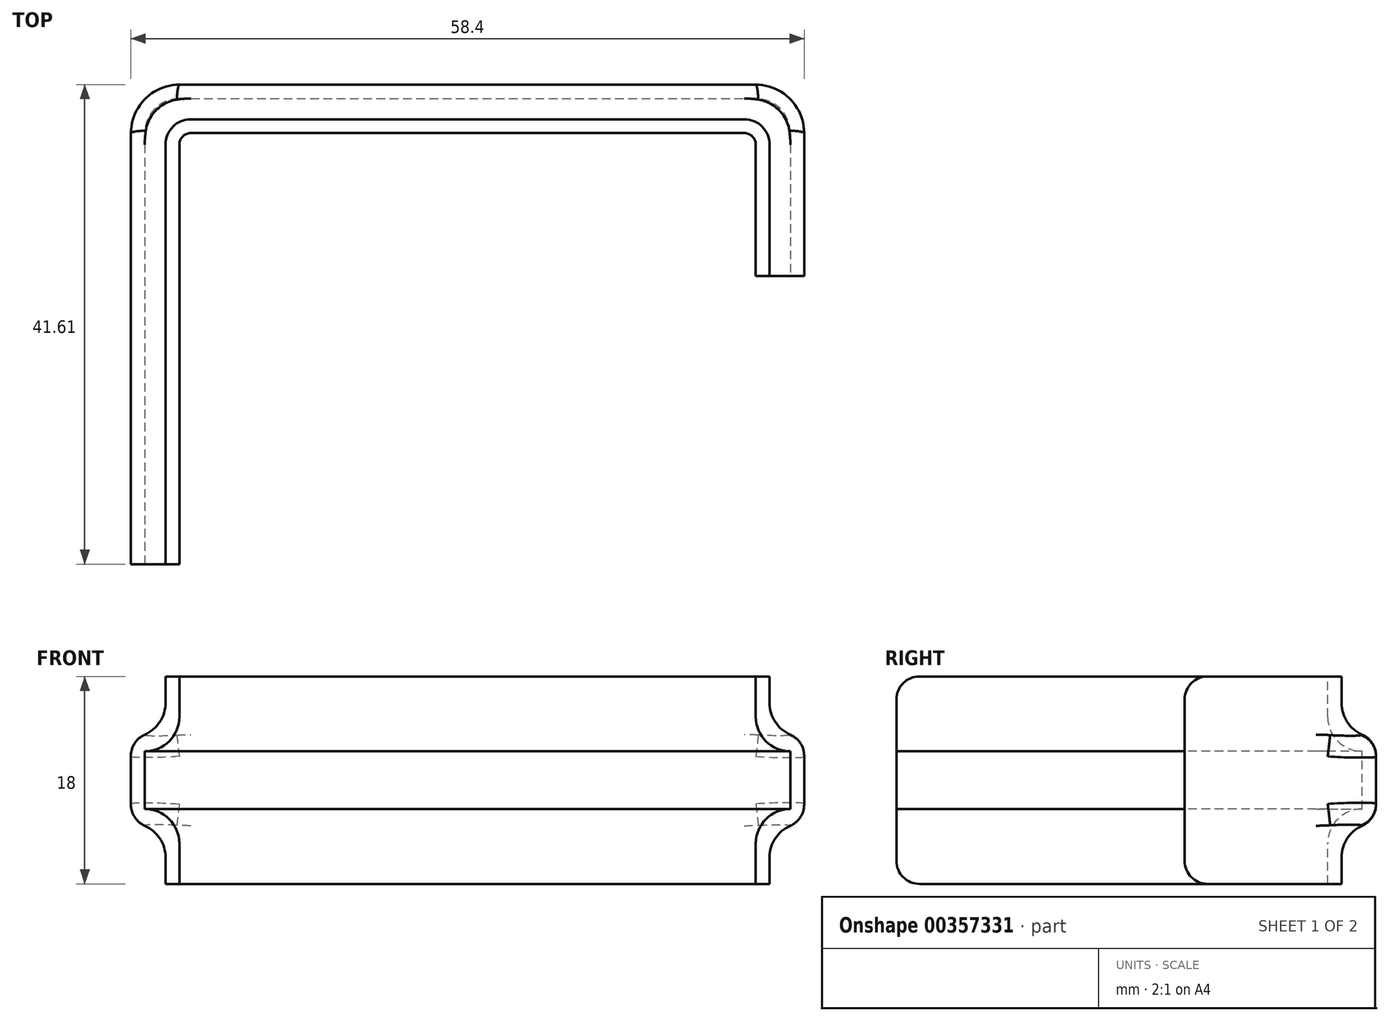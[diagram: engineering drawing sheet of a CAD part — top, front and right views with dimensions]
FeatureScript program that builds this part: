
annotation { "Feature Type Name" : "Feature", "Feature Type Description" : "" }
export const myFeature = defineFeature(function(context is Context, id is Id, definition is map)
    precondition{}
    {
        {
            var Q0;
            Q0=qCreatedBy(makeId("Top.planeOp"),FACE);
            var sketch = newSketch(context, id + "F0", { "sketchPlane" : qUnion([Q0])});
            skLineSegment(sketch, "E0.bottom", {"start": v(-25, 9) * mm, "end": v(-5.6, 9) * mm});
            skLineSegment(sketch, "E0.top", {"start": v(-35, -9) * mm, "end": v(-5.6, -9) * mm});
            skLineSegment(sketch, "E0.right", {"start": v(0, 3.4) * mm, "end": v(0, -3.4) * mm});
            skArc(sketch, "E1", {"start": v(1.67, 7.14) * mm, "mid": v(1.77, 10.77) * mm, "end": v(-1.86, 10.67) * mm, "construction": true});
            skArc(sketch, "E2", {"start": v(-1.86, -10.67) * mm, "mid": v(1.77, -10.77) * mm, "end": v(1.67, -7.14) * mm, "construction": true});
            skPoint(sketch, "E3.visualSharp", {"position": v(-2.5, 9) * mm});
            skArc(sketch, "E3.filletArc", {"start": v(-5.6, 9) * mm, "mid": v(-3.55, 9.44) * mm, "end": v(-1.86, 10.67) * mm, "construction": true});
            skPoint(sketch, "E4.visualSharp", {"position": v(0, 6.5) * mm});
            skArc(sketch, "E4.filletArc", {"start": v(1.67, 7.14) * mm, "mid": v(0.44, 5.45) * mm, "end": v(0, 3.4) * mm, "construction": true});
            skPoint(sketch, "E5.visualSharp", {"position": v(0, -6.5) * mm});
            skArc(sketch, "E5.filletArc", {"start": v(0, -3.4) * mm, "mid": v(0.44, -5.45) * mm, "end": v(1.67, -7.14) * mm, "construction": true});
            skPoint(sketch, "E6.visualSharp", {"position": v(-2.5, -9) * mm});
            skArc(sketch, "E6.filletArc", {"start": v(-1.86, -10.67) * mm, "mid": v(-3.55, -9.44) * mm, "end": v(-5.6, -9) * mm, "construction": true});
            skLineSegment(sketch, "E7", {"start": v(-5.6, 9) * mm, "end": v(0, 9) * mm});
            skLineSegment(sketch, "E8", {"start": v(0, 9) * mm, "end": v(0, 3.4) * mm});
            skLineSegment(sketch, "E9", {"start": v(0, -3.4) * mm, "end": v(0, -9) * mm});
            skLineSegment(sketch, "E10", {"start": v(0, -9) * mm, "end": v(-5.6, -9) * mm});
            skSolve(sketch);
        }
        {
            var Q0;
            Q0=qCreatedBy(makeId("Front.planeOp"),FACE);
            var sketch = newSketch(context, id + "F1", { "sketchPlane" : qUnion([Q0])});
            skLineSegment(sketch, "E11.bottom", {"start": v(3, 2.5) * mm, "end": v(0, 2.5) * mm});
            skLineSegment(sketch, "E11.top", {"start": v(3, -2.5) * mm, "end": v(0, -2.5) * mm});
            skLineSegment(sketch, "E11.left", {"start": v(3, 2.5) * mm, "end": v(3, -2.5) * mm});
            skLineSegment(sketch, "E11.right", {"start": v(0, 2.5) * mm, "end": v(0, -2.5) * mm, "construction": true});
            skLineSegment(sketch, "E12", {"start": v(0, 2.5) * mm, "end": v(0, 9) * mm});
            skLineSegment(sketch, "E13", {"start": v(0, -2.5) * mm, "end": v(0, -9) * mm});
            skLineSegment(sketch, "E14.0", {"start": v(1.2, 3.7) * mm, "end": v(1.2, 9) * mm});
            skLineSegment(sketch, "E14.1", {"start": v(1.2, -3.7) * mm, "end": v(1.2, -9) * mm});
            skLineSegment(sketch, "E14.2", {"start": v(4.2, -3.7) * mm, "end": v(1.2, -3.7) * mm});
            skLineSegment(sketch, "E14.3", {"start": v(4.2, 3.7) * mm, "end": v(4.2, -3.7) * mm});
            skLineSegment(sketch, "E14.4", {"start": v(4.2, 3.7) * mm, "end": v(1.2, 3.7) * mm});
            skLineSegment(sketch, "E15", {"start": v(0, 9) * mm, "end": v(1.2, 9) * mm});
            skLineSegment(sketch, "E16", {"start": v(0, -9) * mm, "end": v(1.2, -9) * mm});
            skSolve(sketch);
        }
        {
            var Q0;
            Q0=makeQuery(id+"F1.imprint","IMPRINT",FACE,{"disambiguationData":[TD([[makeQuery(id+"F1.imprint","IMPRINT",EDGE,{"derivedFrom":sQuery(id+"F1.wireOp",EDGE,"E11.bottom")}),-1.0]])]});
            var Q1;
            Q1=sQuery(id+"F0.wireOp",EDGE,"E0.right");
            var Q2;
            Q2=sQuery(id+"F0.wireOp",EDGE,"E8");
            var Q3;
            Q3=sQuery(id+"F0.wireOp",EDGE,"E7");
            var Q4;
            Q4=sQuery(id+"F0.wireOp",EDGE,"E0.bottom");
            sweep(context, id + "F2", {"profiles" : qUnion([Q0]), "path" : qUnion([Q1, Q2, Q3, Q4])});
        }
        {
            var Q0;
            Q0=makeQuery(id+"F2.opSweep","MID_CAP_EDGE",EDGE,{"disambiguationData":[OSD([sQuery(id+"F0.wireOp",VERTEX,"E7.end"),sQuery(id+"F1.wireOp",EDGE,"E13")])],"capPos":2.0});
            var Q1;
            Q1=makeQuery(id+"F2.opSweep","MID_CAP_EDGE",EDGE,{"disambiguationData":[OSD([sQuery(id+"F0.wireOp",VERTEX,"E7.end"),sQuery(id+"F1.wireOp",EDGE,"E12")])],"capPos":2.0});
            fillet(context, id + "F3", {"entities" : qUnion([Q0, Q1]), "radius" : 1 * mm, "tangentPropagation" : true, "allowEdgeOverflow" : false});
        }
        {
            var Q0;
            Q0=makeQuery(id+"F2.opSweep","MID_CAP_EDGE",EDGE,{"disambiguationData":[OSD([sQuery(id+"F0.wireOp",VERTEX,"E7.end"),sQuery(id+"F1.wireOp",EDGE,"E14.1")])],"capPos":2.0});
            var Q1;
            Q1=makeQuery(id+"F2.opSweep","MID_CAP_EDGE",EDGE,{"disambiguationData":[OSD([sQuery(id+"F0.wireOp",VERTEX,"E7.end"),sQuery(id+"F1.wireOp",EDGE,"E14.0")])],"capPos":2.0});
            fillet(context, id + "F4", {"entities" : qUnion([Q0, Q1]), "radius" : 2.2 * mm, "tangentPropagation" : true, "allowEdgeOverflow" : false});
        }
        {
            var Q0;
            Q0=makeQuery(id+"F2.opSweep","SWEPT_EDGE",EDGE,{"disambiguationData":[OSD([sQuery(id+"F0.wireOp",EDGE,"E0.right"),sQuery(id+"F1.wireOp",EDGE,"E14.1"),sQuery(id+"F1.wireOp",EDGE,"E14.2")])]});
            var Q1;
            Q1=makeQuery(id+"F2.opSweep","SWEPT_EDGE",EDGE,{"disambiguationData":[OSD([sQuery(id+"F0.wireOp",EDGE,"E0.right"),sQuery(id+"F1.wireOp",EDGE,"E11.top"),sQuery(id+"F1.wireOp",EDGE,"E13")])]});
            var Q2;
            Q2=makeQuery(id+"F2.opSweep","SWEPT_EDGE",EDGE,{"disambiguationData":[OSD([sQuery(id+"F0.wireOp",EDGE,"E7"),sQuery(id+"F1.wireOp",EDGE,"E14.0"),sQuery(id+"F1.wireOp",EDGE,"E14.4")])]});
            var Q3;
            Q3=makeQuery(id+"F2.opSweep","SWEPT_EDGE",EDGE,{"disambiguationData":[OSD([sQuery(id+"F0.wireOp",EDGE,"E0.right"),sQuery(id+"F1.wireOp",EDGE,"E11.bottom"),sQuery(id+"F1.wireOp",EDGE,"E12")])]});
            fillet(context, id + "F5", {"entities" : qUnion([Q0, Q1, Q2, Q3]), "radius" : 3 * mm, "tangentPropagation" : true, "allowEdgeOverflow" : false});
        }
        {
            var Q0;
            Q0=makeQuery(id+"F2.opSweep","MID_CAP_EDGE",EDGE,{"disambiguationData":[OSD([sQuery(id+"F0.wireOp",VERTEX,"E7.end"),sQuery(id+"F1.wireOp",EDGE,"E11.left")])],"capPos":2.0});
            fillet(context, id + "F6", {"entities" : qUnion([Q0]), "radius" : 3 * mm, "tangentPropagation" : true, "allowEdgeOverflow" : false});
        }
        {
            var Q0;
            Q0=makeQuery(id+"F2.opSweep","MID_CAP_EDGE",EDGE,{"disambiguationData":[OSD([sQuery(id+"F0.wireOp",VERTEX,"E7.end"),sQuery(id+"F1.wireOp",EDGE,"E14.3")])],"capPos":2.0});
            fillet(context, id + "F7", {"entities" : qUnion([Q0]), "radius" : 4.2 * mm, "tangentPropagation" : true, "allowEdgeOverflow" : false});
        }
        {
            var Q0;
            Q0=makeQuery(id+"F5.opFillet","BLEND_EDGE",EDGE,{"blendedFrom":[makeQuery(id+"F2.opSweep","SWEPT_EDGE",EDGE,{"disambiguationData":[OSD([sQuery(id+"F0.wireOp",EDGE,"E0.right"),sQuery(id+"F1.wireOp",EDGE,"E14.0"),sQuery(id+"F1.wireOp",EDGE,"E14.4")])]}),makeQuery(id+"F2.opSweep","SWEPT_FACE",FACE,{"disambiguationData":[OSD([sQuery(id+"F0.wireOp",EDGE,"E8"),sQuery(id+"F1.wireOp",EDGE,"E14.3")])]})],"blendedInto":[makeQuery(id+"F2.opSweep","SWEPT_FACE",FACE,{"disambiguationData":[OSD([sQuery(id+"F0.wireOp",EDGE,"E8"),sQuery(id+"F1.wireOp",EDGE,"E14.3")])]})]});
            var Q1;
            Q1=makeQuery(id+"F5.opFillet","BLEND_EDGE",EDGE,{"blendedFrom":[makeQuery(id+"F2.opSweep","SWEPT_EDGE",EDGE,{"disambiguationData":[OSD([sQuery(id+"F0.wireOp",EDGE,"E0.right"),sQuery(id+"F1.wireOp",EDGE,"E14.1"),sQuery(id+"F1.wireOp",EDGE,"E14.2")])]}),makeQuery(id+"F2.opSweep","SWEPT_FACE",FACE,{"disambiguationData":[OSD([sQuery(id+"F0.wireOp",EDGE,"E8"),sQuery(id+"F1.wireOp",EDGE,"E14.3")])]})],"blendedInto":[makeQuery(id+"F2.opSweep","SWEPT_FACE",FACE,{"disambiguationData":[OSD([sQuery(id+"F0.wireOp",EDGE,"E8"),sQuery(id+"F1.wireOp",EDGE,"E14.3")])]})]});
            fillet(context, id + "F8", {"entities" : qUnion([Q0, Q1]), "radius" : 2 * mm, "tangentPropagation" : true, "allowEdgeOverflow" : false});
        }
        {
            var Q0;
            Q0=makeQuery(id+"F2.opSweep","SWEPT_BODY",BODY,{"disambiguationData":[OSD([sQuery(id+"F0.wireOp",EDGE,"E0.bottom"),sQuery(id+"F1.wireOp",EDGE,"E11.bottom"),sQuery(id+"F1.wireOp",EDGE,"E11.top"),sQuery(id+"F1.wireOp",EDGE,"E11.left"),sQuery(id+"F1.wireOp",EDGE,"E12"),sQuery(id+"F1.wireOp",EDGE,"E13"),sQuery(id+"F1.wireOp",EDGE,"E14.0"),sQuery(id+"F1.wireOp",EDGE,"E14.1"),sQuery(id+"F1.wireOp",EDGE,"E14.2"),sQuery(id+"F1.wireOp",EDGE,"E14.3"),sQuery(id+"F1.wireOp",EDGE,"E14.4"),sQuery(id+"F1.wireOp",EDGE,"E15"),sQuery(id+"F1.wireOp",EDGE,"E16")])]});
            var Q1;
            Q1=makeQuery(id+"F2.opSweep","CAP_FACE",FACE,{"disambiguationData":[OSD([sQuery(id+"F0.wireOp",VERTEX,"E0.right.end"),sQuery(id+"F1.wireOp",EDGE,"E11.bottom"),sQuery(id+"F1.wireOp",EDGE,"E11.top"),sQuery(id+"F1.wireOp",EDGE,"E11.left"),sQuery(id+"F1.wireOp",EDGE,"E12"),sQuery(id+"F1.wireOp",EDGE,"E13"),sQuery(id+"F1.wireOp",EDGE,"E14.0"),sQuery(id+"F1.wireOp",EDGE,"E14.1"),sQuery(id+"F1.wireOp",EDGE,"E14.2"),sQuery(id+"F1.wireOp",EDGE,"E14.3"),sQuery(id+"F1.wireOp",EDGE,"E14.4"),sQuery(id+"F1.wireOp",EDGE,"E15"),sQuery(id+"F1.wireOp",EDGE,"E16")])],"isStart":true});
            mirror(context, id + "F9", {"operationType" : NewBodyOperationType.ADD, "entities" : qUnion([Q0]), "mirrorPlane" : qUnion([Q1])});
        }
        {
            var Q0;
            Q0=makeQuery(id+"F9.opPattern","COPY",FACE,{"derivedFrom":makeQuery(id+"F2.opSweep","CAP_FACE",FACE,{"disambiguationData":[OSD([sQuery(id+"F0.wireOp",VERTEX,"E0.bottom.start"),sQuery(id+"F1.wireOp",EDGE,"E11.bottom"),sQuery(id+"F1.wireOp",EDGE,"E11.top"),sQuery(id+"F1.wireOp",EDGE,"E11.left"),sQuery(id+"F1.wireOp",EDGE,"E12"),sQuery(id+"F1.wireOp",EDGE,"E13"),sQuery(id+"F1.wireOp",EDGE,"E14.0"),sQuery(id+"F1.wireOp",EDGE,"E14.1"),sQuery(id+"F1.wireOp",EDGE,"E14.2"),sQuery(id+"F1.wireOp",EDGE,"E14.3"),sQuery(id+"F1.wireOp",EDGE,"E14.4"),sQuery(id+"F1.wireOp",EDGE,"E15"),sQuery(id+"F1.wireOp",EDGE,"E16")])],"isStart":false}),"instanceName":"1"});
            extrude(context, id + "F10", {"entities" : qUnion([Q0]), "operationType" : NewBodyOperationType.ADD, "depth" : 25 * mm});
        }
        {
            var Q0;
            Q0=makeQuery(id+"F2.opSweep","CAP_EDGE",EDGE,{"disambiguationData":[OSD([sQuery(id+"F0.wireOp",VERTEX,"E0.bottom.start"),sQuery(id+"F1.wireOp",EDGE,"E16")])],"isStart":false});
            var Q1;
            Q1=makeQuery(id+"F2.opSweep","CAP_EDGE",EDGE,{"disambiguationData":[OSD([sQuery(id+"F0.wireOp",VERTEX,"E0.bottom.start"),sQuery(id+"F1.wireOp",EDGE,"E15")])],"isStart":false});
            var Q2;
            Q2=makeQuery(id+"F10.opExtrude","CAP_EDGE",EDGE,{"disambiguationData":[OSD([sQuery(id+"F0.wireOp",VERTEX,"E0.bottom.start"),sQuery(id+"F1.wireOp",EDGE,"E16")])],"isStart":false});
            var Q3;
            Q3=makeQuery(id+"F10.opExtrude","CAP_EDGE",EDGE,{"disambiguationData":[OSD([sQuery(id+"F0.wireOp",VERTEX,"E0.bottom.start"),sQuery(id+"F1.wireOp",EDGE,"E15")])],"isStart":false});
            fillet(context, id + "F11", {"entities" : qUnion([Q0, Q1, Q2, Q3]), "radius" : 2 * mm, "tangentPropagation" : true, "allowEdgeOverflow" : false});
        }
    });
